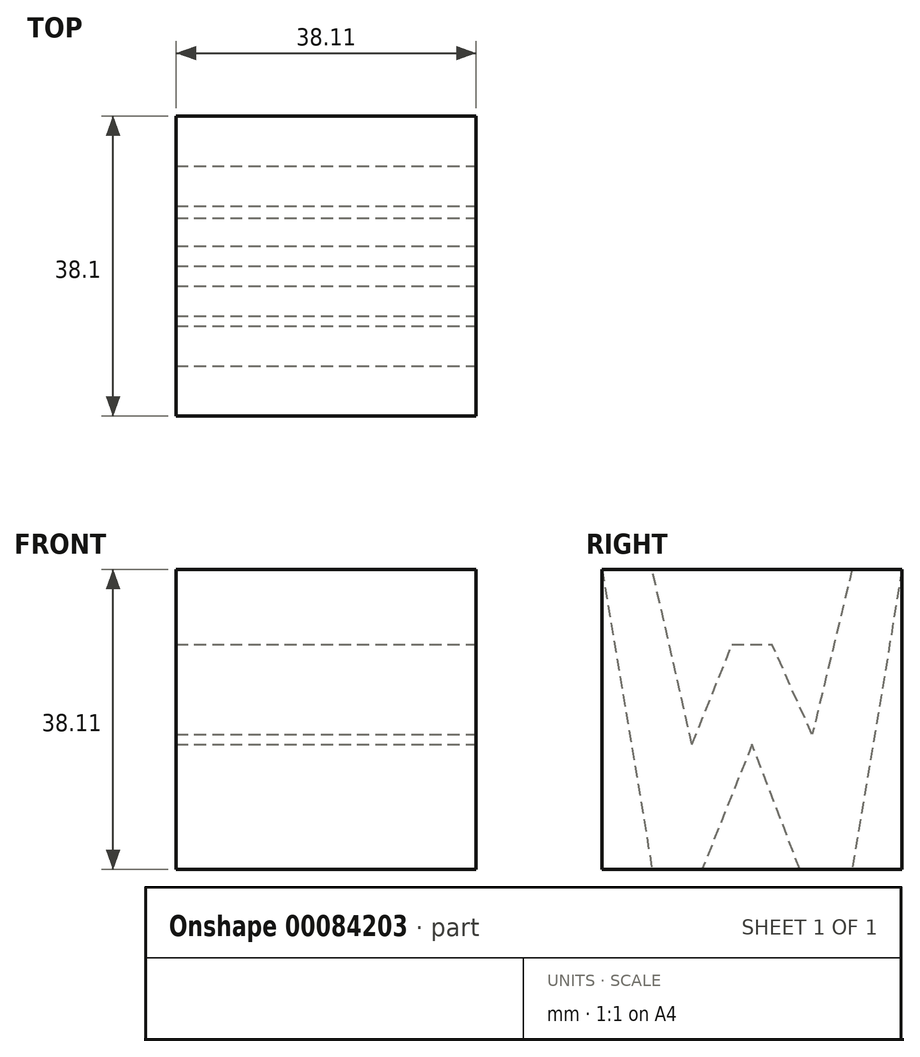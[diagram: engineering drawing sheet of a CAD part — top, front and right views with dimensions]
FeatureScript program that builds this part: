
annotation { "Feature Type Name" : "Feature", "Feature Type Description" : "" }
export const myFeature = defineFeature(function(context is Context, id is Id, definition is map)
    precondition{}
    {
        {
            var Q0;
            Q0=qCreatedBy(makeId("Front.planeOp"),FACE);
            var sketch = newSketch(context, id + "F0", { "sketchPlane" : qUnion([Q0])});
            skLineSegment(sketch, "E0", {"start": v(0, 0) * mm, "end": v(38.11, 0) * mm});
            skLineSegment(sketch, "E1", {"start": v(38.11, 0) * mm, "end": v(38.11, 38.11) * mm});
            skLineSegment(sketch, "E2", {"start": v(38.11, 38.11) * mm, "end": v(0, 38.11) * mm});
            skLineSegment(sketch, "E3", {"start": v(0, 38.11) * mm, "end": v(0, 0) * mm});
            skSolve(sketch);
        }
        {
            var Q0;
            Q0=makeQuery(id+"F0.imprint","IMPRINT",FACE,{"disambiguationData":[TD([[makeQuery(id+"F0.imprint","IMPRINT",EDGE,{"derivedFrom":sQuery(id+"F0.wireOp",EDGE,"E0")}),1.0]])]});
            extrude(context, id + "F1", {"entities" : qUnion([Q0]), "depth" : 38.1 * mm});
        }
        {
            var Q0;
            Q0=qCreatedBy(makeId("Right.planeOp"),FACE);
            cPlane(context, id + "F2", {"entities" : qUnion([Q0]), "cplaneType" : CPlaneType.OFFSET, "offset" : 38.1 * mm, "width" : 152.4 * mm, "height" : 152.4 * mm});
        }
        {
            var Q0;
            Q0=qCreatedBy(id+"F2.planeOp",FACE);
            var sketch = newSketch(context, id + "F3", { "sketchPlane" : qUnion([Q0])});
            skLineSegment(sketch, "E4", {"start": v(0, 0) * mm, "end": v(0, 38.1) * mm});
            skLineSegment(sketch, "E5", {"start": v(0, 38.1) * mm, "end": v(-38.1, 38.1) * mm});
            skLineSegment(sketch, "E6", {"start": v(-38.1, 38.1) * mm, "end": v(-38.1, 0) * mm});
            skLineSegment(sketch, "E7", {"start": v(-38.1, 0) * mm, "end": v(0, 0) * mm});
            skLineSegment(sketch, "E8", {"start": v(-38.1, 38.1) * mm, "end": v(-31.75, 0) * mm});
            skLineSegment(sketch, "E9", {"start": v(-6.35, 38.1) * mm, "end": v(-11.43, 17.12) * mm});
            skLineSegment(sketch, "E10", {"start": v(-11.43, 17.12) * mm, "end": v(-16.51, 28.57) * mm});
            skLineSegment(sketch, "E11", {"start": v(-26.67, 15.88) * mm, "end": v(-31.75, 38.1) * mm});
            skLineSegment(sketch, "E12", {"start": v(-31.75, 38.1) * mm, "end": v(-37.57, 38.11) * mm});
            skLineSegment(sketch, "E13", {"start": v(-6.35, 38.1) * mm, "end": v(0, 38.1) * mm});
            skLineSegment(sketch, "E14", {"start": v(-26.67, 15.87) * mm, "end": v(-21.59, 28.57) * mm});
            skLineSegment(sketch, "E15", {"start": v(-21.59, 28.57) * mm, "end": v(-16.51, 28.57) * mm});
            skLineSegment(sketch, "E16", {"start": v(-12.98, 0) * mm, "end": v(-12.98, 0) * mm});
            skLineSegment(sketch, "E17", {"start": v(-12.98, 0) * mm, "end": v(-19.05, 15.87) * mm});
            skLineSegment(sketch, "E18", {"start": v(-19.05, 15.87) * mm, "end": v(-25.4, 0) * mm});
            skLineSegment(sketch, "E19", {"start": v(-25.4, 0) * mm, "end": v(-31.75, 0) * mm});
            skLineSegment(sketch, "E20", {"start": v(0, 38.1) * mm, "end": v(-6.35, 0) * mm});
            skSolve(sketch);
        }
        {
            var Q0;
            {var subQ0=sQuery(id+"F3.wireOp",EDGE,"E4");Q0=makeQuery(id+"F3.imprint","IMPRINT",FACE,{"disambiguationData":[TD([[makeQuery(id+"F3.imprint","IMPRINT",EDGE,{"derivedFrom":subQ0}),1.0]])]});}
            var Q1;
            {var subQ1=sQuery(id+"F3.wireOp",EDGE,"E9");Q1=makeQuery(id+"F3.imprint","IMPRINT",FACE,{"disambiguationData":[TD([[makeQuery(id+"F3.imprint","IMPRINT",EDGE,{"derivedFrom":subQ1}),-1.0]])]});}
            var Q2;
            {var subQ0=sQuery(id+"F3.wireOp",EDGE,"E6");Q2=makeQuery(id+"F3.imprint","IMPRINT",FACE,{"disambiguationData":[TD([[makeQuery(id+"F3.imprint","IMPRINT",EDGE,{"derivedFrom":subQ0}),1.0]])]});}
            var Q3;
            {var subQ0=sQuery(id+"F3.wireOp",EDGE,"E17");Q3=makeQuery(id+"F3.imprint","IMPRINT",FACE,{"disambiguationData":[TD([[makeQuery(id+"F3.imprint","IMPRINT",EDGE,{"derivedFrom":subQ0}),1.0]])]});}
            extrude(context, id + "F4", {"entities" : qUnion([Q0, Q1, Q2, Q3]), "operationType" : NewBodyOperationType.REMOVE, "oppositeDirection" : true, "depth" : 38.1 * mm});
        }
    });
